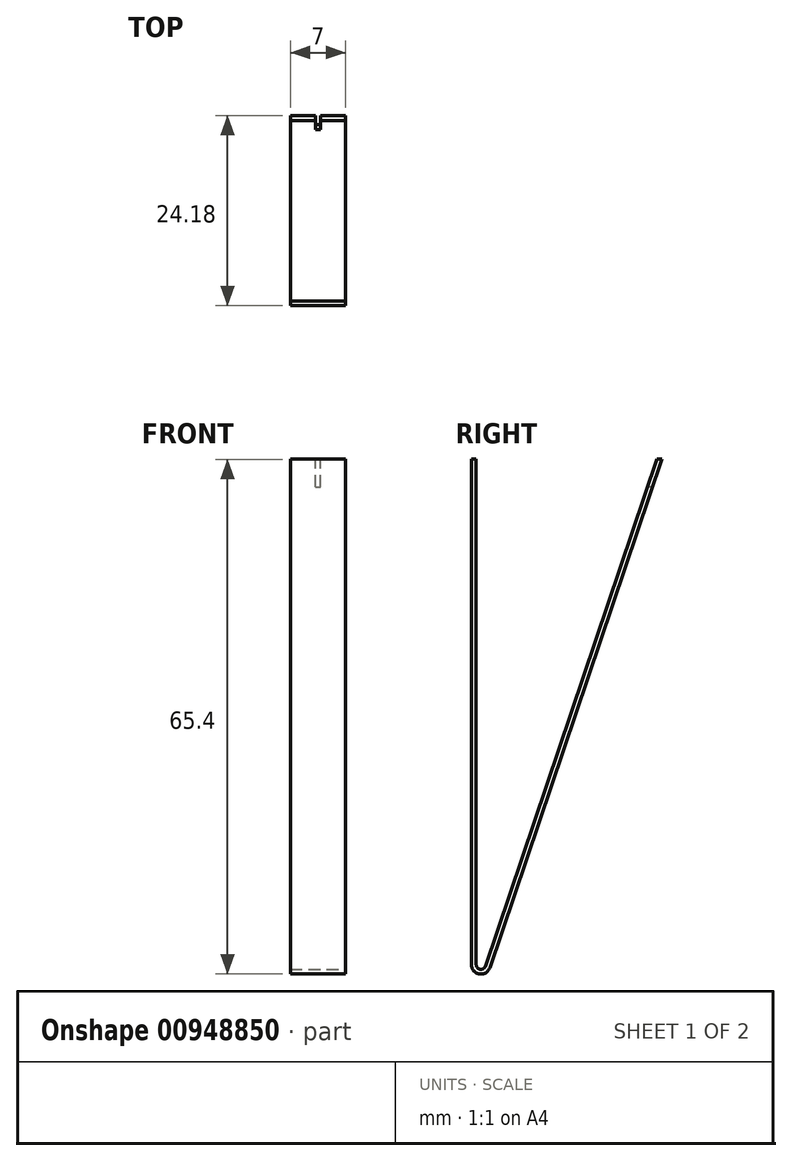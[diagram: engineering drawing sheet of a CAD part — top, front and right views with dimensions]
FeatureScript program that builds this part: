
annotation { "Feature Type Name" : "Feature", "Feature Type Description" : "" }
export const myFeature = defineFeature(function(context is Context, id is Id, definition is map)
    precondition{}
    {
        {
            var Q0;
            Q0=qCreatedBy(makeId("Right.planeOp"),FACE);
            var sketch = newSketch(context, id + "F0", { "sketchPlane" : qUnion([Q0])});
            skLineSegment(sketch, "E0", {"start": v(-47.52, 55.2) * mm, "end": v(-47.52, -16.3) * mm});
            skLineSegment(sketch, "E1", {"start": v(-47.52, -16.3) * mm, "end": v(-23.34, 55.2) * mm});
            skLineSegment(sketch, "E2", {"start": v(-47.52, 51.7) * mm, "end": v(-24.52, 51.7) * mm, "construction": true});
            skLineSegment(sketch, "E3.0", {"start": v(-46.92, -12.65) * mm, "end": v(-23.97, 55.2) * mm});
            skLineSegment(sketch, "E3.1", {"start": v(-46.92, 55.2) * mm, "end": v(-46.92, -12.65) * mm});
            skLineSegment(sketch, "E4", {"start": v(-47.52, 55.2) * mm, "end": v(-46.92, 55.2) * mm});
            skLineSegment(sketch, "E5", {"start": v(-23.34, 55.2) * mm, "end": v(-23.97, 55.2) * mm});
            skSolve(sketch);
        }
        {
            var Q0;
            Q0 = qSketchRegion(id + "F0", true);
            extrude(context, id + "F1", {"entities" : qUnion([Q0]), "depth" : 7 * mm, "offsetDistance" : 25 * mm});
        }
        {
            var Q0;
            Q0=makeQuery(id+"F1.opExtrude","SWEPT_FACE",FACE,{"disambiguationData":[OSD([sQuery(id+"F0.wireOp",EDGE,"E3.1")])]});
            var sketch = newSketch(context, id + "F2", { "sketchPlane" : qUnion([Q0])});
            skLineSegment(sketch, "E6.bottom", {"start": v(-3.2, 51.7) * mm, "end": v(-3.8, 51.7) * mm});
            skLineSegment(sketch, "E6.top", {"start": v(-3.2, 58.7) * mm, "end": v(-3.8, 58.7) * mm});
            skLineSegment(sketch, "E6.left", {"start": v(-3.2, 51.7) * mm, "end": v(-3.2, 58.7) * mm});
            skLineSegment(sketch, "E6.right", {"start": v(-3.8, 51.7) * mm, "end": v(-3.8, 58.7) * mm});
            skPoint(sketch, "E6.middle", {"position": v(-3.5, 55.2) * mm});
            skSolve(sketch);
        }
        {
            var Q0;
            {var subQ0=sQuery(id+"F2.wireOp",EDGE,"E6.bottom");Q0=makeQuery(id+"F2.imprint","IMPRINT",FACE,{"disambiguationData":[TD([[makeQuery(id+"F2.imprint","IMPRINT",EDGE,{"derivedFrom":subQ0}),-1.0]])]});}
            var Q1;
            Q1=sQuery(id+"F2.wireOp",EDGE,"E6.right");
            extrude(context, id + "F3", {"entities" : qUnion([Q0]), "operationType" : NewBodyOperationType.REMOVE, "surfaceEntities" : qUnion([Q1]), "depth" : 32.5 * mm, "offsetDistance" : 25 * mm});
        }
        {
            var Q0;
            Q0=makeQuery(id+"F1.opExtrude","SWEPT_EDGE",EDGE,{"disambiguationData":[OSD([sQuery(id+"F0.wireOp",EDGE,"E3.0"),sQuery(id+"F0.wireOp",EDGE,"E3.1")])]});
            fillet(context, id + "F4", {"entities" : qUnion([Q0]), "radius" : 0.6 * mm, "tangentPropagation" : true, "allowEdgeOverflow" : false});
        }
        {
            var Q0;
            Q0=makeQuery(id+"F1.opExtrude","SWEPT_EDGE",EDGE,{"disambiguationData":[OSD([sQuery(id+"F0.wireOp",EDGE,"E0"),sQuery(id+"F0.wireOp",EDGE,"E1")])]});
            fillet(context, id + "F5", {"entities" : qUnion([Q0]), "radius" : 1.2 * mm, "tangentPropagation" : true, "allowEdgeOverflow" : false});
        }
    });
